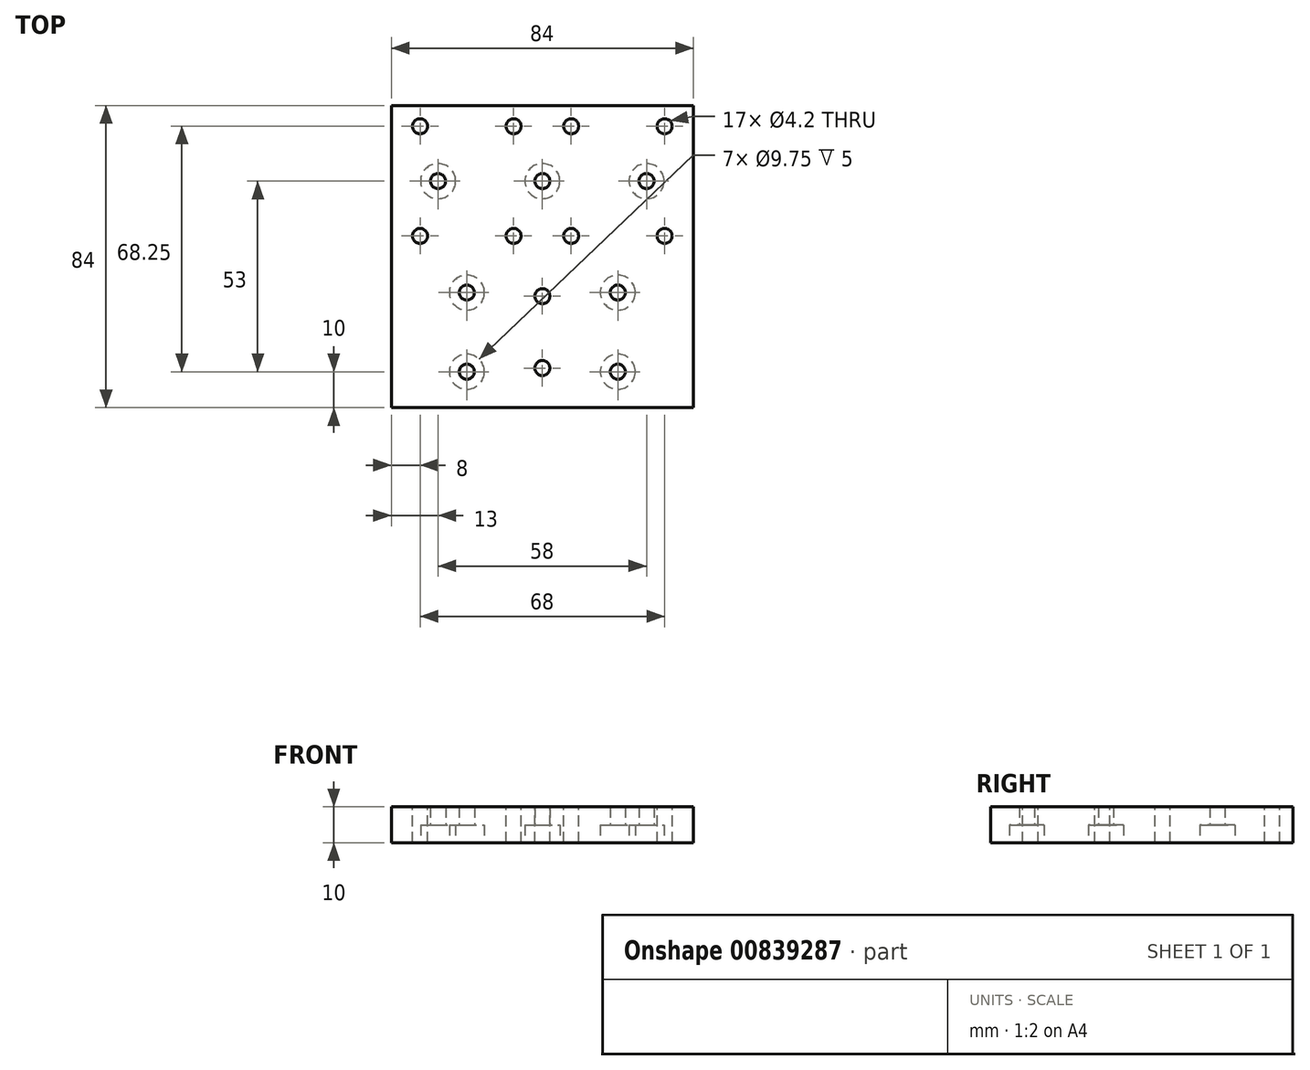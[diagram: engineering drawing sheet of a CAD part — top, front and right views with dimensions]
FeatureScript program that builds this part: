
annotation { "Feature Type Name" : "Feature", "Feature Type Description" : "" }
export const myFeature = defineFeature(function(context is Context, id is Id, definition is map)
    precondition{}
    {
        {
            var Q0;
            Q0=qCreatedBy(makeId("Top.planeOp"),FACE);
            var sketch = newSketch(context, id + "F0", { "sketchPlane" : qUnion([Q0])});
            skLineSegment(sketch, "E0.bottom", {"start": v(42, -42) * mm, "end": v(-42, -42) * mm});
            skLineSegment(sketch, "E0.top", {"start": v(42, 42) * mm, "end": v(-42, 42) * mm});
            skLineSegment(sketch, "E0.left", {"start": v(42, -42) * mm, "end": v(42, 42) * mm});
            skLineSegment(sketch, "E0.right", {"start": v(-42, -42) * mm, "end": v(-42, 42) * mm});
            skPoint(sketch, "E0.middle", {"position": v(0, 0) * mm});
            skSolve(sketch);
        }
        {
            var Q0;
            Q0=makeQuery(id+"F0.imprint","IMPRINT",FACE,{"disambiguationData":[TD([[makeQuery(id+"F0.imprint","IMPRINT",EDGE,{"derivedFrom":sQuery(id+"F0.wireOp",EDGE,"E0.bottom")}),-1.0]])]});
            extrude(context, id + "F1", {"entities" : qUnion([Q0]), "depth" : 10 * mm, "offsetDistance" : 25 * mm});
        }
        {
            var Q0;
            Q0=makeQuery(id+"F1.opExtrude","CAP_FACE",FACE,{"disambiguationData":[OSD([sQuery(id+"F0.wireOp",EDGE,"E0.bottom"),sQuery(id+"F0.wireOp",EDGE,"E0.top"),sQuery(id+"F0.wireOp",EDGE,"E0.left"),sQuery(id+"F0.wireOp",EDGE,"E0.right")])],"isStart":false});
            var sketch = newSketch(context, id + "F2", { "sketchPlane" : qUnion([Q0])});
            skCircle(sketch, "E1", {"center": v(-34, 36.25) * mm, "radius": 2.15 * mm});
            skCircle(sketch, "E2.0.1.0", {"center": v(-34, 5.75) * mm, "radius": 2.15 * mm});
            skCircle(sketch, "E2.1.0.0", {"center": v(-8, 36.25) * mm, "radius": 2.15 * mm});
            skCircle(sketch, "E2.1.1.0", {"center": v(-8, 5.75) * mm, "radius": 2.15 * mm});
            skLineSegment(sketch, "E2.direction1", {"start": v(-34, 36.25) * mm, "end": v(-8, 36.25) * mm, "construction": true});
            skLineSegment(sketch, "E2.direction2", {"start": v(-34, 36.25) * mm, "end": v(-34, 5.75) * mm, "construction": true});
            skCircle(sketch, "E3.MirrorC", {"center": v(34, 36.25) * mm, "radius": 2.15 * mm});
            skLineSegment(sketch, "E4.MirrorCS", {"start": v(34, 36.25) * mm, "end": v(34, 5.75) * mm, "construction": true});
            skCircle(sketch, "E5.MirrorC", {"center": v(8, 5.75) * mm, "radius": 2.15 * mm});
            skCircle(sketch, "E6.MirrorC", {"center": v(8, 36.25) * mm, "radius": 2.15 * mm});
            skCircle(sketch, "E7.MirrorC", {"center": v(34, 5.75) * mm, "radius": 2.15 * mm});
            skLineSegment(sketch, "E8.MirrorCS", {"start": v(34, 36.25) * mm, "end": v(8, 36.25) * mm, "construction": true});
            skCircle(sketch, "E9", {"center": v(0, -31) * mm, "radius": 2.15 * mm});
            skCircle(sketch, "E10", {"center": v(0, -11) * mm, "radius": 2.15 * mm});
            skLineSegment(sketch, "E11", {"start": v(0, -11) * mm, "end": v(0, -31) * mm});
            skPoint(sketch, "E12", {"position": v(0, -21) * mm});
            skSolve(sketch);
        }
        {
            var Q0;
            Q0=sQuery(id+"F2.wireOp",VERTEX,"E2.direction1.start");
            var Q1;
            Q1=sQuery(id+"F2.wireOp",VERTEX,"E2.direction1.end");
            var Q2;
            Q2=sQuery(id+"F2.wireOp",VERTEX,"E8.MirrorCS.end");
            var Q3;
            Q3=sQuery(id+"F2.wireOp",VERTEX,"E4.MirrorCS.start");
            var Q4;
            Q4=sQuery(id+"F2.wireOp",VERTEX,"E4.MirrorCS.end");
            var Q5;
            Q5=sQuery(id+"F2.wireOp",VERTEX,"E5.MirrorC.center");
            var Q6;
            Q6=sQuery(id+"F2.wireOp",VERTEX,"E2.1.1.0.center");
            var Q7;
            Q7=sQuery(id+"F2.wireOp",VERTEX,"E2.direction2.end");
            var Q8;
            Q8=sQuery(id+"F2.wireOp",VERTEX,"E11.start");
            var Q9;
            Q9=sQuery(id+"F2.wireOp",VERTEX,"E11.end");
            var Q10;
            Q10=makeQuery(id+"F1.opExtrude","SWEPT_BODY",BODY,{"disambiguationData":[OSD([sQuery(id+"F0.wireOp",EDGE,"E0.bottom"),sQuery(id+"F0.wireOp",EDGE,"E0.top"),sQuery(id+"F0.wireOp",EDGE,"E0.left"),sQuery(id+"F0.wireOp",EDGE,"E0.right")])]});
            hole(context, id + "F3", {"style" : HoleStyle.SIMPLE, "endStyle" : HoleEndStyle.THROUGH, "standardTappedOrClearance" : lookupTablePath({ "standard" : "ISO", "engagement" : "75%", "pitch" : "0.8 mm", "size" : "M5", "type" : "Tapped" }), "standardBlindInLast" : lookupTablePath({ "standard" : "ISO", "fit" : "Normal", "engagement" : "75%", "pitch" : "0.8 mm", "size" : "M5", "type" : "Clearance & tapped" }), "holeDiameter" : 4.2 * mm, "majorDiameter" : 5 * mm, "showTappedDepth" : true, "isTappedThrough" : true, "tappedDepth" : 12 * mm, "tapClearance" : 3, "locations" : qUnion([Q0, Q1, Q2, Q3, Q4, Q5, Q6, Q7, Q8, Q9]), "scope" : qUnion([Q10])});
        }
        {
            var Q0;
            Q0=makeQuery(id+"F1.opExtrude","CAP_FACE",FACE,{"disambiguationData":[OSD([sQuery(id+"F0.wireOp",EDGE,"E0.bottom"),sQuery(id+"F0.wireOp",EDGE,"E0.top"),sQuery(id+"F0.wireOp",EDGE,"E0.left"),sQuery(id+"F0.wireOp",EDGE,"E0.right")])],"isStart":true});
            var sketch = newSketch(context, id + "F4", { "sketchPlane" : qUnion([Q0])});
            skLineSegment(sketch, "E13", {"start": v(0, -42) * mm, "end": v(0, 0) * mm});
            skPoint(sketch, "E14", {"position": v(-29, -21) * mm});
            skPoint(sketch, "E14.positionSnap0", {"position": v(0, -21) * mm});
            skPoint(sketch, "E15.MirrorP", {"position": v(29, -21) * mm});
            skPoint(sketch, "E16", {"position": v(21, 10) * mm});
            skPoint(sketch, "E17", {"position": v(21, 32) * mm});
            skPoint(sketch, "E18.MirrorP", {"position": v(-21, 32) * mm});
            skPoint(sketch, "E19.MirrorP", {"position": v(-21, 10) * mm});
            skSolve(sketch);
        }
        {
            var Q0;
            Q0=sQuery(id+"F4.wireOp",VERTEX,"E15.MirrorP");
            var Q1;
            Q1=sQuery(id+"F4.wireOp",VERTEX,"E14.positionSnap0");
            var Q2;
            Q2=sQuery(id+"F4.wireOp",VERTEX,"E14");
            var Q3;
            Q3=sQuery(id+"F4.wireOp",VERTEX,"d88d07f4-aeb3-49de-aa75-ca476e4ecd1a");
            var Q4;
            Q4=sQuery(id+"F4.wireOp",VERTEX,"e825e703-b8aa-4643-b370-3f793b8301e8");
            var Q5;
            Q5=sQuery(id+"F4.wireOp",VERTEX,"b0c4f517-99a4-474b-ae3d-2e51fd7c01770.MirrorP");
            var Q6;
            Q6=sQuery(id+"F4.wireOp",VERTEX,"4b2d6f30-5abc-4886-bac1-71261c3135fe0.MirrorP");
            var Q7;
            Q7=sQuery(id+"F4.wireOp",VERTEX,"E16");
            var Q8;
            Q8=sQuery(id+"F4.wireOp",VERTEX,"E17");
            var Q9;
            Q9=sQuery(id+"F4.wireOp",VERTEX,"E18.MirrorP");
            var Q10;
            Q10=sQuery(id+"F4.wireOp",VERTEX,"E19.MirrorP");
            var Q11;
            Q11=makeQuery(id+"F1.opExtrude","SWEPT_BODY",BODY,{"disambiguationData":[OSD([sQuery(id+"F0.wireOp",EDGE,"E0.bottom"),sQuery(id+"F0.wireOp",EDGE,"E0.top"),sQuery(id+"F0.wireOp",EDGE,"E0.left"),sQuery(id+"F0.wireOp",EDGE,"E0.right")])]});
            hole(context, id + "F5", {"style" : HoleStyle.C_BORE, "endStyle" : HoleEndStyle.THROUGH, "standardTappedOrClearance" : lookupTablePath({ "standard" : "ISO", "engagement" : "75%", "pitch" : "0.8 mm", "size" : "M5", "type" : "Tapped" }), "standardBlindInLast" : lookupTablePath({ "standard" : "ISO", "fit" : "Normal", "engagement" : "75%", "pitch" : "0.8 mm", "size" : "M5", "type" : "Clearance & tapped" }), "holeDiameter" : 4.2 * mm, "cBoreDiameter" : 9.75 * mm, "cBoreDepth" : 5 * mm, "majorDiameter" : 5 * mm, "showTappedDepth" : true, "isTappedThrough" : true, "tappedDepth" : 12 * mm, "tapClearance" : 3, "locations" : qUnion([Q0, Q1, Q2, Q3, Q4, Q5, Q6, Q7, Q8, Q9, Q10]), "scope" : qUnion([Q11])});
        }
    });
